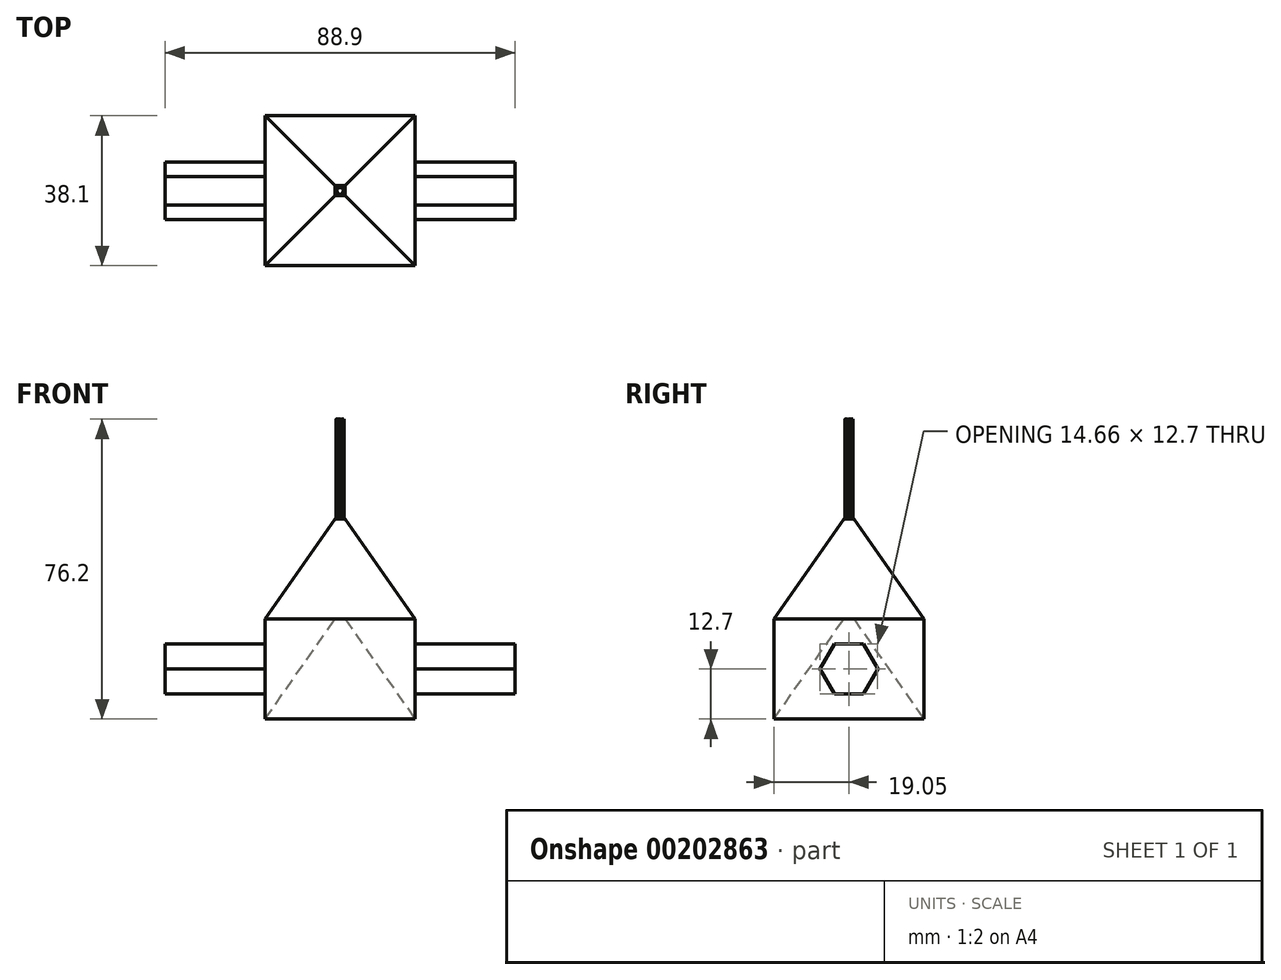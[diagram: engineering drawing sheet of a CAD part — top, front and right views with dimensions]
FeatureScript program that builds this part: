
annotation { "Feature Type Name" : "Feature", "Feature Type Description" : "" }
export const myFeature = defineFeature(function(context is Context, id is Id, definition is map)
    precondition{}
    {
        {
            var Q0;
            Q0=qCreatedBy(makeId("Top.planeOp"),FACE);
            var sketch = newSketch(context, id + "F0", { "sketchPlane" : qUnion([Q0])});
            skLineSegment(sketch, "E0.bottom", {"start": v(-19.05, 19.05) * mm, "end": v(19.05, 19.05) * mm});
            skLineSegment(sketch, "E0.top", {"start": v(-19.05, -19.05) * mm, "end": v(19.05, -19.05) * mm});
            skLineSegment(sketch, "E0.left", {"start": v(-19.05, 19.05) * mm, "end": v(-19.05, -19.05) * mm});
            skLineSegment(sketch, "E0.right", {"start": v(19.05, 19.05) * mm, "end": v(19.05, -19.05) * mm});
            skPoint(sketch, "E0.middle", {"position": v(0, 0) * mm});
            skSolve(sketch);
        }
        {
            var Q0;
            Q0 = qSketchRegion(id + "F0", true);
            extrude(context, id + "F1", {"entities" : qUnion([Q0]), "depth" : 25.4 * mm, "hasDraft" : true, "draftAngle" : 35 * degree, "draftPullDirection" : true});
        }
        {
            var Q0;
            Q0=makeQuery(id+"F1.opExtrude","CAP_FACE",FACE,{"disambiguationData":[OSD([sQuery(id+"F0.wireOp",EDGE,"E0.bottom"),sQuery(id+"F0.wireOp",EDGE,"E0.top"),sQuery(id+"F0.wireOp",EDGE,"E0.left"),sQuery(id+"F0.wireOp",EDGE,"E0.right")])],"isStart":true});
            extrude(context, id + "F2", {"entities" : qUnion([Q0]), "operationType" : NewBodyOperationType.ADD, "depth" : 25.4 * mm});
        }
        {
            var Q0;
            Q0=makeQuery(id+"F2.opExtrude","CAP_FACE",FACE,{"disambiguationData":[OSD([sQuery(id+"F0.wireOp",EDGE,"E0.bottom"),sQuery(id+"F0.wireOp",EDGE,"E0.top"),sQuery(id+"F0.wireOp",EDGE,"E0.left"),sQuery(id+"F0.wireOp",EDGE,"E0.right")])],"isStart":false});
            extrude(context, id + "F3", {"entities" : qUnion([Q0]), "operationType" : NewBodyOperationType.REMOVE, "oppositeDirection" : true, "depth" : 25.4 * mm, "hasDraft" : true, "draftAngle" : 35 * degree, "draftPullDirection" : true});
        }
        {
            var Q0;
            Q0=qCreatedBy(makeId("Front.planeOp"),FACE);
            var sketch = newSketch(context, id + "F4", { "sketchPlane" : qUnion([Q0])});
            skPoint(sketch, "E1", {"position": v(-75.5, 53) * mm});
            skSolve(sketch);
        }
        {
            var Q0;
            Q0=qCreatedBy(makeId("Top.planeOp"),FACE);
            var sketch = newSketch(context, id + "F5", { "sketchPlane" : qUnion([Q0])});
            skLineSegment(sketch, "E2", {"start": v(-63.31, 50.97) * mm, "end": v(-25.27, 31.51) * mm});
            skSolve(sketch);
        }
        {
            var Q0;
            Q0=makeQuery(id+"F2.opExtrude","SWEPT_FACE",FACE,{"disambiguationData":[OSD([sQuery(id+"F0.wireOp",EDGE,"E0.left")])]});
            var sketch = newSketch(context, id + "F6", { "sketchPlane" : qUnion([Q0])});
            skCircle(sketch, "E3.cCircle", {"center": v(0, -12.7) * mm, "radius": 6.35 * mm, "construction": true});
            skLineSegment(sketch, "E3.0", {"start": v(-3.67, -6.35) * mm, "end": v(3.67, -6.35) * mm});
            skLineSegment(sketch, "E3.1", {"start": v(3.67, -6.35) * mm, "end": v(7.33, -12.7) * mm});
            skLineSegment(sketch, "E3.2", {"start": v(7.33, -12.7) * mm, "end": v(3.67, -19.05) * mm});
            skLineSegment(sketch, "E3.3", {"start": v(3.67, -19.05) * mm, "end": v(-3.67, -19.05) * mm});
            skLineSegment(sketch, "E3.4", {"start": v(-3.67, -19.05) * mm, "end": v(-7.33, -12.7) * mm});
            skLineSegment(sketch, "E3.5", {"start": v(-7.33, -12.7) * mm, "end": v(-3.67, -6.35) * mm});
            skPoint(sketch, "E3.0.midPoint", {"position": v(0, -6.35) * mm});
            skLineSegment(sketch, "E4", {"start": v(0, -12.7) * mm, "end": v(0, -25.4) * mm, "construction": true});
            skLineSegment(sketch, "E5", {"start": v(0, -12.7) * mm, "end": v(19.05, -12.7) * mm, "construction": true});
            skSolve(sketch);
        }
        {
            var Q0;
            Q0 = qSketchRegion(id + "F6", true);
            extrude(context, id + "F7", {"entities" : qUnion([Q0]), "depth" : 25.4 * mm});
        }
        {
            var Q0;
            Q0=makeQuery(id+"F7.opExtrude","SWEPT_BODY",BODY,{"disambiguationData":[OSD([sQuery(id+"F6.wireOp",EDGE,"E3.0"),sQuery(id+"F6.wireOp",EDGE,"E3.1"),sQuery(id+"F6.wireOp",EDGE,"E3.2"),sQuery(id+"F6.wireOp",EDGE,"E3.3"),sQuery(id+"F6.wireOp",EDGE,"E3.4"),sQuery(id+"F6.wireOp",EDGE,"E3.5")])]});
            var Q1;
            Q1=qCreatedBy(makeId("Right.planeOp"),FACE);
            mirror(context, id + "F8", {"operationType" : NewBodyOperationType.ADD, "entities" : qUnion([Q0]), "mirrorPlane" : qUnion([Q1])});
        }
        {
            var Q0;
            Q0=makeQuery(id+"F1.opExtrude","CAP_FACE",FACE,{"disambiguationData":[OSD([sQuery(id+"F0.wireOp",EDGE,"E0.bottom"),sQuery(id+"F0.wireOp",EDGE,"E0.top"),sQuery(id+"F0.wireOp",EDGE,"E0.left"),sQuery(id+"F0.wireOp",EDGE,"E0.right")])],"isStart":false});
            var sketch = newSketch(context, id + "F9", { "sketchPlane" : qUnion([Q0])});
            skCircle(sketch, "E6", {"center": v(0, 0) * mm, "radius": 0.89 * mm, "construction": true});
            skCircle(sketch, "E7", {"center": v(0, 0.89) * mm, "radius": 0.13 * mm});
            skCircle(sketch, "E8.1.0", {"center": v(-0.44, 0.77) * mm, "radius": 0.13 * mm});
            skCircle(sketch, "E8.2.0", {"center": v(-0.77, 0.44) * mm, "radius": 0.13 * mm});
            skCircle(sketch, "E8.3.0", {"center": v(-0.89, 0) * mm, "radius": 0.13 * mm});
            skCircle(sketch, "E8.4.0", {"center": v(-0.77, -0.44) * mm, "radius": 0.13 * mm});
            skCircle(sketch, "E8.5.0", {"center": v(-0.44, -0.77) * mm, "radius": 0.13 * mm});
            skCircle(sketch, "E8.6.0", {"center": v(0, -0.89) * mm, "radius": 0.13 * mm});
            skCircle(sketch, "E8.7.0", {"center": v(0.44, -0.77) * mm, "radius": 0.13 * mm});
            skCircle(sketch, "E8.8.0", {"center": v(0.77, -0.44) * mm, "radius": 0.13 * mm});
            skCircle(sketch, "E8.9.0", {"center": v(0.89, 0) * mm, "radius": 0.13 * mm});
            skCircle(sketch, "E8.10.0", {"center": v(0.77, 0.44) * mm, "radius": 0.13 * mm});
            skCircle(sketch, "E8.11.0", {"center": v(0.44, 0.77) * mm, "radius": 0.13 * mm});
            skSolve(sketch);
        }
        {
            var Q0;
            Q0 = qSketchRegion(id + "F9", true);
            extrude(context, id + "F10", {"entities" : qUnion([Q0]), "operationType" : NewBodyOperationType.ADD, "depth" : 25.4 * mm});
        }
    });
